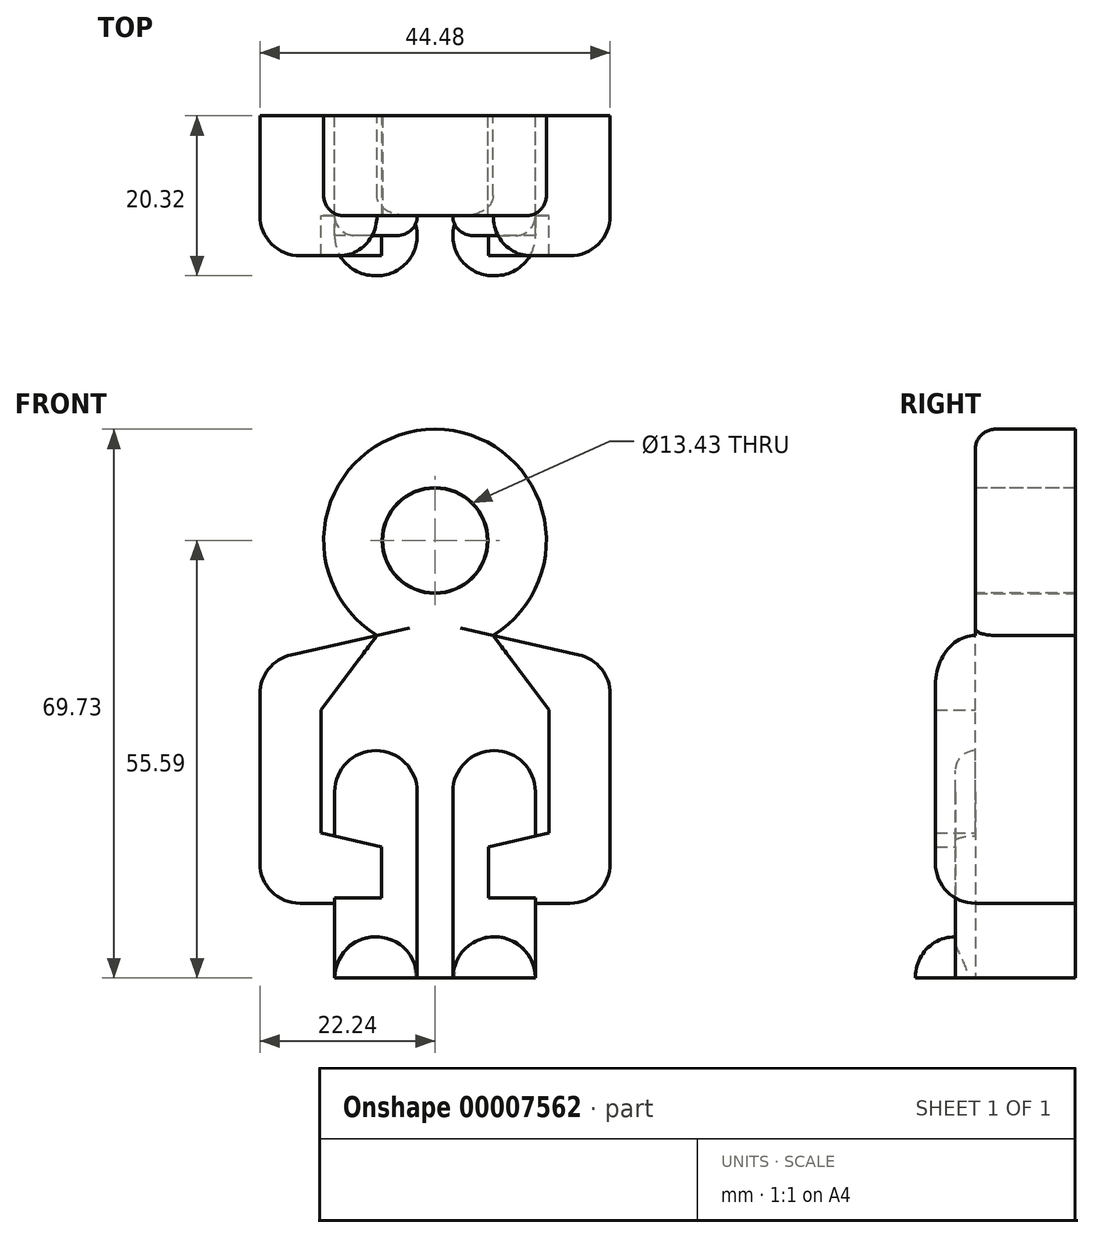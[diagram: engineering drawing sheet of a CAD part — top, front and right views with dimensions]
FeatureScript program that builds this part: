
annotation { "Feature Type Name" : "Feature", "Feature Type Description" : "" }
export const myFeature = defineFeature(function(context is Context, id is Id, definition is map)
    precondition{}
    {
        {
            var Q0;
            Q0=qCreatedBy(makeId("Front.planeOp"),FACE);
            var sketch = newSketch(context, id + "F0", { "sketchPlane" : qUnion([Q0])});
            skCircle(sketch, "E0", {"center": v(0, 0) * mm, "radius": 6.71 * mm});
            skCircle(sketch, "E1", {"center": v(0, 0) * mm, "radius": 14.14 * mm});
            skLineSegment(sketch, "E2", {"start": v(-7.38, -12.06) * mm, "end": v(-22.24, -15.41) * mm});
            skLineSegment(sketch, "E3", {"start": v(-22.24, -15.41) * mm, "end": v(-22.24, -46.1) * mm});
            skLineSegment(sketch, "E4", {"start": v(-22.24, -46.1) * mm, "end": v(-12.75, -46.1) * mm});
            skLineSegment(sketch, "E5", {"start": v(-12.75, -46.1) * mm, "end": v(-12.75, -26.8) * mm});
            skLineSegment(sketch, "E6", {"start": v(-12.75, -26.8) * mm, "end": v(-12.75, -55.59) * mm});
            skLineSegment(sketch, "E7", {"start": v(-12.75, -55.59) * mm, "end": v(0, -55.59) * mm});
            skLineSegment(sketch, "E8", {"start": v(0, -55.59) * mm, "end": v(0, 0) * mm});
            skLineSegment(sketch, "E9.MirrorCS", {"start": v(7.38, -12.06) * mm, "end": v(22.24, -15.41) * mm});
            skLineSegment(sketch, "E10.MirrorCS", {"start": v(22.24, -15.41) * mm, "end": v(22.24, -46.1) * mm});
            skLineSegment(sketch, "E11.MirrorCS", {"start": v(12.75, -26.8) * mm, "end": v(12.75, -55.59) * mm});
            skLineSegment(sketch, "E12.MirrorCS", {"start": v(22.24, -46.1) * mm, "end": v(12.75, -46.1) * mm});
            skLineSegment(sketch, "E13.MirrorCS", {"start": v(12.75, -55.59) * mm, "end": v(0, -55.59) * mm});
            skSolve(sketch);
        }
        {
            var Q0;
            Q0 = qSketchRegion(id + "F0", true);
            extrude(context, id + "F1", {"entities" : qUnion([Q0]), "depth" : 25.4 * mm});
        }
        {
            var Q0;
            Q0=makeQuery(id+"F1.opExtrude","SWEPT_EDGE",EDGE,{"disambiguationData":[OSD([sQuery(id+"F0.wireOp",EDGE,"E3"),sQuery(id+"F0.wireOp",EDGE,"E4")])]});
            var Q1;
            Q1=makeQuery(id+"F1.opExtrude","SWEPT_EDGE",EDGE,{"disambiguationData":[OSD([sQuery(id+"F0.wireOp",EDGE,"E10.MirrorCS"),sQuery(id+"F0.wireOp",EDGE,"E12.MirrorCS")])]});
            fillet(context, id + "F2", {"entities" : qUnion([Q0, Q1]), "radius" : 5.08 * mm, "tangentPropagation" : true, "allowEdgeOverflow" : false});
        }
        {
            var Q0;
            Q0=makeQuery(id+"F1.opExtrude","SWEPT_EDGE",EDGE,{"disambiguationData":[OSD([sQuery(id+"F0.wireOp",EDGE,"E2"),sQuery(id+"F0.wireOp",EDGE,"E3")])]});
            var Q1;
            Q1=makeQuery(id+"F1.opExtrude","SWEPT_EDGE",EDGE,{"disambiguationData":[OSD([sQuery(id+"F0.wireOp",EDGE,"E9.MirrorCS"),sQuery(id+"F0.wireOp",EDGE,"E10.MirrorCS")])]});
            fillet(context, id + "F3", {"entities" : qUnion([Q0, Q1]), "radius" : 5.08 * mm, "tangentPropagation" : true, "allowEdgeOverflow" : false});
        }
        {
            var Q0;
            Q0=makeQuery(id+"F1.opExtrude","CAP_FACE",FACE,{"disambiguationData":[OSD([sQuery(id+"F0.wireOp",EDGE,"E0"),sQuery(id+"F0.wireOp",EDGE,"E1"),sQuery(id+"F0.wireOp",EDGE,"E2"),sQuery(id+"F0.wireOp",EDGE,"E3"),sQuery(id+"F0.wireOp",EDGE,"E4"),sQuery(id+"F0.wireOp",EDGE,"E6"),sQuery(id+"F0.wireOp",EDGE,"E7"),sQuery(id+"F0.wireOp",EDGE,"E9.MirrorCS"),sQuery(id+"F0.wireOp",EDGE,"E10.MirrorCS"),sQuery(id+"F0.wireOp",EDGE,"E11.MirrorCS"),sQuery(id+"F0.wireOp",EDGE,"E12.MirrorCS"),sQuery(id+"F0.wireOp",EDGE,"E13.MirrorCS")])],"isStart":false});
            var sketch = newSketch(context, id + "F4", { "sketchPlane" : qUnion([Q0])});
            skLineSegment(sketch, "E14", {"start": v(-12.75, -46.1) * mm, "end": v(-6.77, -46.1) * mm});
            skLineSegment(sketch, "E15", {"start": v(-6.77, -46.1) * mm, "end": v(-6.77, -38.95) * mm});
            skLineSegment(sketch, "E16", {"start": v(-6.77, -38.95) * mm, "end": v(-14.46, -37.13) * mm});
            skLineSegment(sketch, "E17", {"start": v(-14.46, -37.13) * mm, "end": v(-14.46, -21.54) * mm});
            skLineSegment(sketch, "E18", {"start": v(-14.46, -21.54) * mm, "end": v(-7.38, -12.06) * mm});
            skLineSegment(sketch, "E19", {"start": v(0, 0) * mm, "end": v(0, -55.59) * mm});
            skLineSegment(sketch, "E20.MirrorCS", {"start": v(14.46, -21.54) * mm, "end": v(7.38, -12.06) * mm});
            skLineSegment(sketch, "E21.MirrorCS", {"start": v(14.46, -37.13) * mm, "end": v(14.46, -21.54) * mm});
            skLineSegment(sketch, "E22.MirrorCS", {"start": v(6.77, -38.95) * mm, "end": v(14.46, -37.13) * mm});
            skLineSegment(sketch, "E23.MirrorCS", {"start": v(6.77, -46.1) * mm, "end": v(6.77, -38.95) * mm});
            skLineSegment(sketch, "E24.MirrorCS", {"start": v(12.75, -46.1) * mm, "end": v(6.77, -46.1) * mm});
            skLineSegment(sketch, "E25.0", {"start": v(-7.38, -12.06) * mm, "end": v(-18.27, -14.52) * mm});
            skArc(sketch, "E26.0", {"start": v(-18.27, -14.52) * mm, "mid": v(-21.12, -16.3) * mm, "end": v(-22.24, -19.47) * mm});
            skLineSegment(sketch, "E27.0", {"start": v(-22.24, -19.47) * mm, "end": v(-22.24, -41.02) * mm});
            skArc(sketch, "E28.0", {"start": v(-22.24, -41.02) * mm, "mid": v(-20.75, -44.6) * mm, "end": v(-17.16, -46.1) * mm});
            skLineSegment(sketch, "E29.0", {"start": v(-17.16, -46.1) * mm, "end": v(-12.75, -46.1) * mm});
            skLineSegment(sketch, "E30.0", {"start": v(17.16, -46.1) * mm, "end": v(12.75, -46.1) * mm});
            skArc(sketch, "E31.0", {"start": v(17.16, -46.1) * mm, "mid": v(20.75, -44.6) * mm, "end": v(22.24, -41.02) * mm});
            skLineSegment(sketch, "E32.0", {"start": v(22.24, -19.47) * mm, "end": v(22.24, -41.02) * mm});
            skArc(sketch, "E33.0", {"start": v(22.24, -19.47) * mm, "mid": v(21.12, -16.3) * mm, "end": v(18.27, -14.52) * mm});
            skLineSegment(sketch, "E34.0", {"start": v(7.38, -12.06) * mm, "end": v(18.27, -14.52) * mm});
            skSolve(sketch);
        }
        {
            var Q0;
            Q0=makeQuery(id+"F4.imprint","IMPRINT",FACE,{"disambiguationData":[TD([[makeQuery(id+"F4.imprint","IMPRINT",EDGE,{"derivedFrom":sQuery(id+"F4.wireOp",EDGE,"E14")}),1.0]])]});
            var Q1;
            Q1=makeQuery(id+"F4.imprint","IMPRINT",FACE,{"disambiguationData":[TD([[makeQuery(id+"F4.imprint","IMPRINT",EDGE,{"derivedFrom":sQuery(id+"F4.wireOp",EDGE,"E20.MirrorCS")}),-1.0]])]});
            extrude(context, id + "F5", {"entities" : qUnion([Q0, Q1]), "operationType" : NewBodyOperationType.ADD, "depth" : 5.08 * mm});
        }
        {
            var Q0;
            Q0=makeQuery(id+"F5.opExtrude","CAP_EDGE",EDGE,{"disambiguationData":[OSD([sQuery(id+"F4.wireOp",EDGE,"E27.0")])],"isStart":false});
            fillet(context, id + "F6", {"entities" : qUnion([Q0]), "radius" : 5.08 * mm, "tangentPropagation" : true, "allowEdgeOverflow" : false});
        }
        {
            var Q0;
            Q0=makeQuery(id+"F5.opExtrude","CAP_EDGE",EDGE,{"disambiguationData":[OSD([sQuery(id+"F4.wireOp",EDGE,"E32.0")])],"isStart":false});
            fillet(context, id + "F7", {"entities" : qUnion([Q0]), "radius" : 5.08 * mm, "tangentPropagation" : true, "allowEdgeOverflow" : false});
        }
        {
            var Q0;
            Q0=makeQuery(id+"F1.opExtrude","CAP_FACE",FACE,{"disambiguationData":[OSD([sQuery(id+"F0.wireOp",EDGE,"E0"),sQuery(id+"F0.wireOp",EDGE,"E1"),sQuery(id+"F0.wireOp",EDGE,"E2"),sQuery(id+"F0.wireOp",EDGE,"E3"),sQuery(id+"F0.wireOp",EDGE,"E4"),sQuery(id+"F0.wireOp",EDGE,"E6"),sQuery(id+"F0.wireOp",EDGE,"E7"),sQuery(id+"F0.wireOp",EDGE,"E9.MirrorCS"),sQuery(id+"F0.wireOp",EDGE,"E10.MirrorCS"),sQuery(id+"F0.wireOp",EDGE,"E11.MirrorCS"),sQuery(id+"F0.wireOp",EDGE,"E12.MirrorCS"),sQuery(id+"F0.wireOp",EDGE,"E13.MirrorCS")])],"isStart":false});
            var sketch = newSketch(context, id + "F8", { "sketchPlane" : qUnion([Q0])});
            skLineSegment(sketch, "E35", {"start": v(-12.75, -55.59) * mm, "end": v(-12.75, -31.94) * mm});
            skLineSegment(sketch, "E36", {"start": v(-2.26, -31.94) * mm, "end": v(-2.26, -55.59) * mm});
            skLineSegment(sketch, "E37", {"start": v(-2.26, -55.59) * mm, "end": v(-12.75, -55.59) * mm});
            skLineSegment(sketch, "E38", {"start": v(0, 0) * mm, "end": v(0, -6.71) * mm});
            skArc(sketch, "E39", {"start": v(-2.26, -31.94) * mm, "mid": v(-7.5, -26.7) * mm, "end": v(-12.75, -31.94) * mm});
            skArc(sketch, "E40.MirrorCS", {"start": v(2.26, -31.94) * mm, "mid": v(7.5, -26.7) * mm, "end": v(12.75, -31.94) * mm});
            skLineSegment(sketch, "E41.MirrorCS", {"start": v(12.75, -55.59) * mm, "end": v(12.75, -31.94) * mm});
            skLineSegment(sketch, "E42.MirrorCS", {"start": v(2.26, -31.94) * mm, "end": v(2.26, -55.59) * mm});
            skLineSegment(sketch, "E43.MirrorCS", {"start": v(2.26, -55.59) * mm, "end": v(12.75, -55.59) * mm});
            skSolve(sketch);
        }
        {
            var Q0;
            Q0 = qSketchRegion(id + "F8", true);
            extrude(context, id + "F9", {"entities" : qUnion([Q0]), "operationType" : NewBodyOperationType.ADD, "depth" : 2.54 * mm});
        }
        {
            var Q0;
            Q0=makeQuery(id+"F9.opExtrude","CAP_FACE",FACE,{"disambiguationData":[OSD([sQuery(id+"F8.wireOp",EDGE,"E35"),sQuery(id+"F8.wireOp",EDGE,"E36"),sQuery(id+"F8.wireOp",EDGE,"E37"),sQuery(id+"F8.wireOp",EDGE,"E39")])],"isStart":false});
            var sketch = newSketch(context, id + "F10", { "sketchPlane" : qUnion([Q0])});
            skLineSegment(sketch, "E44", {"start": v(-12.75, -55.59) * mm, "end": v(-2.26, -55.59) * mm});
            skLineSegment(sketch, "E45", {"start": v(0, -32.66) * mm, "end": v(0, -61.43) * mm});
            skArc(sketch, "E46", {"start": v(-2.26, -55.59) * mm, "mid": v(-7.5, -50.34) * mm, "end": v(-12.75, -55.59) * mm});
            skArc(sketch, "E47.MirrorCS", {"start": v(2.26, -55.59) * mm, "mid": v(7.5, -50.34) * mm, "end": v(12.75, -55.59) * mm});
            skLineSegment(sketch, "E48.MirrorCS", {"start": v(12.75, -55.59) * mm, "end": v(2.26, -55.59) * mm});
            skSolve(sketch);
        }
        {
            var Q0;
            Q0 = qSketchRegion(id + "F10", true);
            extrude(context, id + "F11", {"entities" : qUnion([Q0]), "operationType" : NewBodyOperationType.ADD, "depth" : 5.08 * mm});
        }
        {
            var Q0;
            Q0=makeQuery(id+"F11.opExtrude","CAP_EDGE",EDGE,{"disambiguationData":[OSD([sQuery(id+"F10.wireOp",EDGE,"E46")])],"isStart":false});
            var Q1;
            Q1=makeQuery(id+"F11.opExtrude","CAP_EDGE",EDGE,{"disambiguationData":[OSD([sQuery(id+"F10.wireOp",EDGE,"E47.MirrorCS")])],"isStart":false});
            fillet(context, id + "F12", {"entities" : qUnion([Q0, Q1]), "radius" : 5.08 * mm, "tangentPropagation" : true, "allowEdgeOverflow" : false});
        }
        {
            var Q0;
            Q0=makeQuery(id+"F9.opExtrude","CAP_EDGE",EDGE,{"disambiguationData":[OSD([sQuery(id+"F8.wireOp",EDGE,"E39")])],"isStart":false});
            fillet(context, id + "F13", {"entities" : qUnion([Q0]), "radius" : 2.54 * mm, "tangentPropagation" : true, "allowEdgeOverflow" : false});
        }
        {
            var Q0;
            Q0=makeQuery(id+"F9.opExtrude","CAP_EDGE",EDGE,{"disambiguationData":[OSD([sQuery(id+"F8.wireOp",EDGE,"E40.MirrorCS")])],"isStart":false});
            fillet(context, id + "F14", {"entities" : qUnion([Q0]), "radius" : 2.54 * mm, "tangentPropagation" : true, "allowEdgeOverflow" : false});
        }
        {
            var Q0;
            Q0=makeQuery(id+"F1.opExtrude","CAP_EDGE",EDGE,{"disambiguationData":[OSD([sQuery(id+"F0.wireOp",EDGE,"E1")])],"isStart":false});
            fillet(context, id + "F15", {"entities" : qUnion([Q0]), "radius" : 2.54 * mm, "tangentPropagation" : true, "allowEdgeOverflow" : false});
        }
        {
            var Q0;
            Q0=makeQuery(id+"F1.opExtrude","CAP_FACE",FACE,{"disambiguationData":[OSD([sQuery(id+"F0.wireOp",EDGE,"E0"),sQuery(id+"F0.wireOp",EDGE,"E1"),sQuery(id+"F0.wireOp",EDGE,"E2"),sQuery(id+"F0.wireOp",EDGE,"E3"),sQuery(id+"F0.wireOp",EDGE,"E4"),sQuery(id+"F0.wireOp",EDGE,"E6"),sQuery(id+"F0.wireOp",EDGE,"E7"),sQuery(id+"F0.wireOp",EDGE,"E9.MirrorCS"),sQuery(id+"F0.wireOp",EDGE,"E10.MirrorCS"),sQuery(id+"F0.wireOp",EDGE,"E11.MirrorCS"),sQuery(id+"F0.wireOp",EDGE,"E12.MirrorCS"),sQuery(id+"F0.wireOp",EDGE,"E13.MirrorCS")])],"isStart":true});
            var sketch = newSketch(context, id + "F16", { "sketchPlane" : qUnion([Q0])});
            skLineSegment(sketch, "E49.0.0", {"start": v(22.24, -41.02) * mm, "end": v(22.24, -19.47) * mm});
            skArc(sketch, "E49.0.1", {"start": v(22.24, -19.47) * mm, "mid": v(21.12, -16.3) * mm, "end": v(18.27, -14.52) * mm});
            skLineSegment(sketch, "E49.0.2", {"start": v(18.27, -14.52) * mm, "end": v(7.38, -12.06) * mm});
            skArc(sketch, "E49.0.3", {"start": v(7.38, -12.06) * mm, "mid": v(0, 14.14) * mm, "end": v(-7.38, -12.06) * mm});
            skLineSegment(sketch, "E49.0.4", {"start": v(-7.38, -12.06) * mm, "end": v(-18.27, -14.52) * mm});
            skArc(sketch, "E49.0.5", {"start": v(-18.27, -14.52) * mm, "mid": v(-21.12, -16.3) * mm, "end": v(-22.24, -19.47) * mm});
            skLineSegment(sketch, "E49.0.6", {"start": v(-22.24, -19.47) * mm, "end": v(-22.24, -41.02) * mm});
            skArc(sketch, "E49.0.7", {"start": v(-22.24, -41.02) * mm, "mid": v(-20.75, -44.6) * mm, "end": v(-17.16, -46.1) * mm});
            skLineSegment(sketch, "E49.0.8", {"start": v(-17.16, -46.1) * mm, "end": v(-12.75, -46.1) * mm});
            skLineSegment(sketch, "E49.0.9", {"start": v(-12.75, -46.1) * mm, "end": v(-12.75, -55.59) * mm});
            skLineSegment(sketch, "E49.0.10", {"start": v(-12.75, -55.59) * mm, "end": v(12.75, -55.59) * mm});
            skLineSegment(sketch, "E49.0.11", {"start": v(12.75, -55.59) * mm, "end": v(12.75, -46.1) * mm});
            skLineSegment(sketch, "E49.0.12", {"start": v(12.75, -46.1) * mm, "end": v(17.16, -46.1) * mm});
            skArc(sketch, "E49.0.13", {"start": v(17.16, -46.1) * mm, "mid": v(20.75, -44.6) * mm, "end": v(22.24, -41.02) * mm});
            skCircle(sketch, "E50.0", {"center": v(0, 0) * mm, "radius": 6.71 * mm});
            skSolve(sketch);
        }
        {
            var Q0;
            Q0 = qSketchRegion(id + "F16", true);
            extrude(context, id + "F17", {"entities" : qUnion([Q0]), "operationType" : NewBodyOperationType.REMOVE, "oppositeDirection" : true, "depth" : 12.7 * mm});
        }
        {
            var Q0;
            Q0=makeQuery(id+"F1.opExtrude","CAP_FACE",FACE,{"disambiguationData":[OSD([sQuery(id+"F0.wireOp",EDGE,"E0"),sQuery(id+"F0.wireOp",EDGE,"E1"),sQuery(id+"F0.wireOp",EDGE,"E2"),sQuery(id+"F0.wireOp",EDGE,"E3"),sQuery(id+"F0.wireOp",EDGE,"E4"),sQuery(id+"F0.wireOp",EDGE,"E6"),sQuery(id+"F0.wireOp",EDGE,"E7"),sQuery(id+"F0.wireOp",EDGE,"E9.MirrorCS"),sQuery(id+"F0.wireOp",EDGE,"E10.MirrorCS"),sQuery(id+"F0.wireOp",EDGE,"E11.MirrorCS"),sQuery(id+"F0.wireOp",EDGE,"E12.MirrorCS"),sQuery(id+"F0.wireOp",EDGE,"E13.MirrorCS")])],"isStart":false});
            var sketch = newSketch(context, id + "F18", { "sketchPlane" : qUnion([Q0])});
            skCircle(sketch, "E51", {"center": v(0, 0) * mm, "radius": 6.66 * mm});
            skSolve(sketch);
        }
        {
            var Q0;
            Q0 = qSketchRegion(id + "F18", true);
            extrude(context, id + "F19", {"entities" : qUnion([Q0]), "oppositeDirection" : true, "depth" : 12.7 * mm});
        }
    });
